# Revit family: Касетный блок VRF системы
name_source: partatom
category: Mechanical Equipment
revit_build: Autodesk Revit 2016 (Build: 20150506_1715(x64)
units: mm (PartAtom-declared; Revit-internal decimal feet)

## family parameters
Cut with Voids When Loaded = No
Host = Face
Part Type = Normal
Room Calculation Point = No
Round Connector Dimension = Use Diameter
Shared = No

## types (6) — shared parameters
Default Elevation = 1219.2 mm  [stored 4 ft]
Артикул планка = 1022725
Вес декоративной планки = 6.00 kg
Высота = 298 mm  [stored 0.97769 ft]
Высота планки = 37 mm  [stored 0.121391 ft]
Глубина = 840 mm  [stored 2.75591 ft]
Глубина планки = 950 mm  [stored 3.1168 ft]
Диаметр газовой трубы = 15.88 mm  [stored 0.0520997 ft]
Диаметр дренажного шлага = 25 mm  [stored 0.082021 ft]
Модель декоративной планки = ESVMCP-SF-950
Наименование = Касетный блок VRF-системы
Наименование декоративной планки = Декоративная панель для кассетного блока
Напор дренажной помпы, мм водяного столба = 850
Номинал предохранителя = 10 A
Производитель = Electrolux
Таблица модель = Модель
Таблица модель планка = Модель планка
Таблица наименование = Наименование
Таблица наименование планка = Наименование планка
Таблица напор дренажной помпы = Напор дренажной помпы
Таблица параметров = Таблица параметров
Таблица параметров планка = Таблица параметров планка
Таблица расход воздуха = Расход воздуха
Таблица тип хладагента = Тип хладагента
Таблица уровень звукового давления = Уровень звукового давления
Таблица электропитание = Электропитание
Фаза = 1
Частота сети = 50 Hz
Ширина = 840 mm  [stored 2.75591 ft]
Ширина планки = 950 mm  [stored 3.1168 ft]
Эл. питание(коннектор) = 220 V
Электропитание, (В) = 220

## per-type parameters (varying)
| type | Артикул | Вес | Диаметр жидкостной трубы | Максимальная потребляемая мощность | Расход воздуха, (м.куб/ч) | Теплопроизводительность | Уровень звукового давления, (Дб(А)) | Холодопроизводительность |
| ESVMC4/C-SF-56 | 1022685 | 23.00 kg | 6.35 mm  [stored 0.0208333 ft] | 0.22 kW | 960-840-720 | 6.50 kW | 32-30-27 | 5.60 kW |
| ESVMC4/C-SF-71 | 1022686 | 23.00 kg | 9.53 mm | 0.22 kW | 1200-1020-900 | 8.50 kW | 33-31-29 | 7.10 kW |
| ESVMC4/C-SF-90 | 1022687 | 24.00 kg | 9.53 mm | 0.22 kW | 1560-1380-1200 | 9.60 kW | 36-34-32 | 8.40 kW |
| ESVMC4/C-SF-112 | 1022688 | 27.00 kg | 9.53 mm | 0.40 kW | 1920-1680-1440 | 13.00 kW | 41-38-35 | 11.20 kW |
| ESVMC4/C-SF-140 | 1022689 | 27.00 kg | 9.53 mm | 0.40 kW | 2040-1740-1500 | 16.30 kW | 44-39-36 | 14.20 kW |
| ESVMC4/C-SF-160 | 1022690 | 27.00 kg | 9.53 mm | 0.40 kW | 2220-1920-1620 | 18.00 kW | 44-42-38 | 16.00 kW |

note: column(s) folded — value = type name in every type: Модель

note: [stored X ft] marks values corroborated as IEEE doubles in the binary element streams (Revit-internal decimal feet)

## geometry (parser evidence)
native form markers: Blend x2
no freeform markers — native parametric forms only
